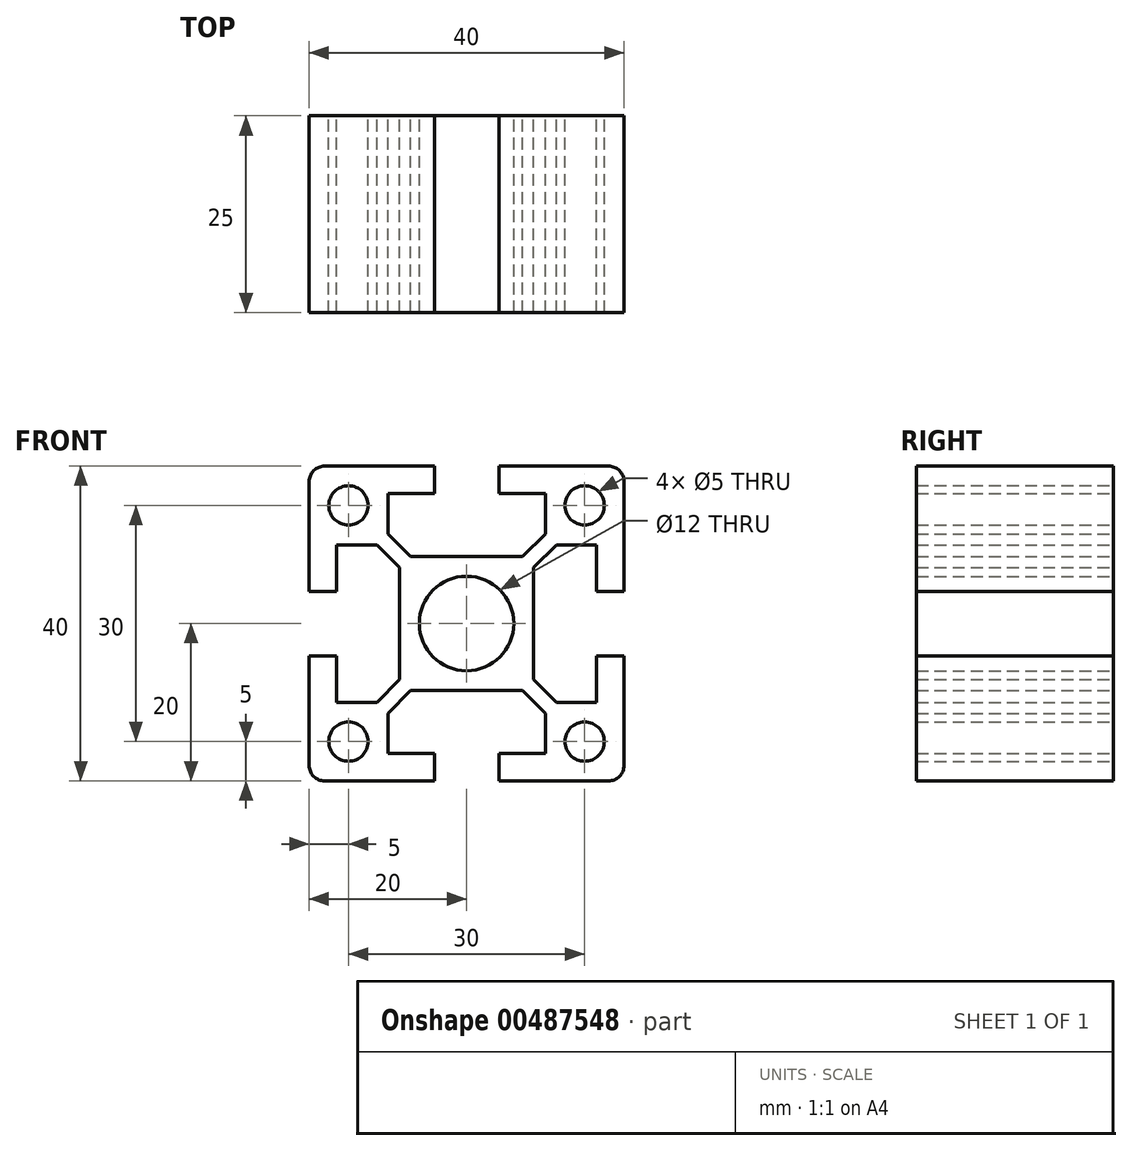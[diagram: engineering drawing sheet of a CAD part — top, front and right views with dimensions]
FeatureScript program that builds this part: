
annotation { "Feature Type Name" : "Feature", "Feature Type Description" : "" }
export const myFeature = defineFeature(function(context is Context, id is Id, definition is map)
    precondition{}
    {
        {
            var Q0;
            Q0=qCreatedBy(makeId("Front.planeOp"),FACE);
            var sketch = newSketch(context, id + "F0", { "sketchPlane" : qUnion([Q0])});
            skLineSegment(sketch, "E0.bottom", {"start": v(20, -20) * mm, "end": v(-20, -20) * mm});
            skLineSegment(sketch, "E0.top", {"start": v(20, 20) * mm, "end": v(-20, 20) * mm});
            skLineSegment(sketch, "E0.left", {"start": v(20, -20) * mm, "end": v(20, 20) * mm});
            skLineSegment(sketch, "E0.right", {"start": v(-20, -20) * mm, "end": v(-20, 20) * mm});
            skPoint(sketch, "E0.middle", {"position": v(0, 0) * mm});
            skCircle(sketch, "E1", {"center": v(0, 0) * mm, "radius": 6 * mm});
            skLineSegment(sketch, "E2", {"start": v(20, 15) * mm, "end": v(-20, 15) * mm, "construction": true});
            skLineSegment(sketch, "E3", {"start": v(20, -15) * mm, "end": v(-20, -15) * mm, "construction": true});
            skLineSegment(sketch, "E4", {"start": v(-15, -20) * mm, "end": v(-15, 20) * mm, "construction": true});
            skLineSegment(sketch, "E5", {"start": v(15, -20) * mm, "end": v(15, 20) * mm, "construction": true});
            skCircle(sketch, "E6", {"center": v(-15, 15) * mm, "radius": 2.5 * mm});
            skCircle(sketch, "E7", {"center": v(-15, -15) * mm, "radius": 2.5 * mm});
            skLineSegment(sketch, "E8", {"start": v(-4.1, 20) * mm, "end": v(-4.1, 16.5) * mm});
            skLineSegment(sketch, "E9", {"start": v(-4.1, 16.5) * mm, "end": v(-10, 16.5) * mm});
            skLineSegment(sketch, "E10", {"start": v(-10, 16.5) * mm, "end": v(-10, 11.4) * mm});
            skLineSegment(sketch, "E11", {"start": v(-10, 11.4) * mm, "end": v(-7.1, 8.5) * mm});
            skLineSegment(sketch, "E12", {"start": v(-7.1, 8.5) * mm, "end": v(0, 8.5) * mm});
            skLineSegment(sketch, "E13", {"start": v(0, 8.5) * mm, "end": v(0, 20) * mm});
            skLineSegment(sketch, "E14.MirrorCS", {"start": v(7.1, 8.5) * mm, "end": v(0, 8.5) * mm});
            skLineSegment(sketch, "E15.MirrorCS", {"start": v(10, 11.4) * mm, "end": v(7.1, 8.5) * mm});
            skLineSegment(sketch, "E16.MirrorCS", {"start": v(10, 16.5) * mm, "end": v(10, 11.4) * mm});
            skLineSegment(sketch, "E17.MirrorCS", {"start": v(4.1, 16.5) * mm, "end": v(10, 16.5) * mm});
            skLineSegment(sketch, "E18.MirrorCS", {"start": v(4.1, 20) * mm, "end": v(4.1, 16.5) * mm});
            skLineSegment(sketch, "E19.MirrorCS", {"start": v(7.1, -8.5) * mm, "end": v(0, -8.5) * mm});
            skLineSegment(sketch, "E20.MirrorCS", {"start": v(10, -11.4) * mm, "end": v(7.1, -8.5) * mm});
            skLineSegment(sketch, "E21.MirrorCS", {"start": v(10, -16.5) * mm, "end": v(10, -11.4) * mm});
            skLineSegment(sketch, "E22.MirrorCS", {"start": v(4.1, -16.5) * mm, "end": v(10, -16.5) * mm});
            skLineSegment(sketch, "E23.MirrorCS", {"start": v(4.1, -20) * mm, "end": v(4.1, -16.5) * mm});
            skLineSegment(sketch, "E24.MirrorCS", {"start": v(-4.1, -20) * mm, "end": v(-4.1, -16.5) * mm});
            skLineSegment(sketch, "E25.MirrorCS", {"start": v(-4.1, -16.5) * mm, "end": v(-10, -16.5) * mm});
            skLineSegment(sketch, "E26.MirrorCS", {"start": v(-10, -16.5) * mm, "end": v(-10, -11.4) * mm});
            skLineSegment(sketch, "E27.MirrorCS", {"start": v(-10, -11.4) * mm, "end": v(-7.1, -8.5) * mm});
            skLineSegment(sketch, "E28.MirrorCS", {"start": v(-7.1, -8.5) * mm, "end": v(0, -8.5) * mm});
            skCircle(sketch, "E29.MirrorC", {"center": v(15, -15) * mm, "radius": 2.5 * mm});
            skCircle(sketch, "E30.MirrorC", {"center": v(15, 15) * mm, "radius": 2.5 * mm});
            skLineSegment(sketch, "E31", {"start": v(-20, -4.1) * mm, "end": v(-16.5, -4.1) * mm});
            skLineSegment(sketch, "E32", {"start": v(-16.5, -4.1) * mm, "end": v(-16.5, -10) * mm});
            skLineSegment(sketch, "E33", {"start": v(-16.5, -10) * mm, "end": v(-11.4, -10) * mm});
            skLineSegment(sketch, "E34", {"start": v(-11.4, -10) * mm, "end": v(-8.5, -7.1) * mm});
            skLineSegment(sketch, "E35", {"start": v(-8.5, -7.1) * mm, "end": v(-8.5, 0) * mm});
            skLineSegment(sketch, "E36", {"start": v(-8.5, 0) * mm, "end": v(-20, 0) * mm});
            skLineSegment(sketch, "E37.MirrorCS", {"start": v(-8.5, 7.1) * mm, "end": v(-8.5, 0) * mm});
            skLineSegment(sketch, "E38.MirrorCS", {"start": v(-11.4, 10) * mm, "end": v(-8.5, 7.1) * mm});
            skLineSegment(sketch, "E39.MirrorCS", {"start": v(-16.5, 10) * mm, "end": v(-11.4, 10) * mm});
            skLineSegment(sketch, "E40.MirrorCS", {"start": v(-16.5, 4.1) * mm, "end": v(-16.5, 10) * mm});
            skLineSegment(sketch, "E41.MirrorCS", {"start": v(-20, 4.1) * mm, "end": v(-16.5, 4.1) * mm});
            skLineSegment(sketch, "E42.MirrorCS", {"start": v(8.5, 7.1) * mm, "end": v(8.5, 0) * mm});
            skLineSegment(sketch, "E43.MirrorCS", {"start": v(8.5, -7.1) * mm, "end": v(8.5, 0) * mm});
            skLineSegment(sketch, "E44.MirrorCS", {"start": v(11.4, -10) * mm, "end": v(8.5, -7.1) * mm});
            skLineSegment(sketch, "E45.MirrorCS", {"start": v(11.4, 10) * mm, "end": v(8.5, 7.1) * mm});
            skLineSegment(sketch, "E46.MirrorCS", {"start": v(16.5, 10) * mm, "end": v(11.4, 10) * mm});
            skLineSegment(sketch, "E47.MirrorCS", {"start": v(16.5, -10) * mm, "end": v(11.4, -10) * mm});
            skLineSegment(sketch, "E48.MirrorCS", {"start": v(16.5, -4.1) * mm, "end": v(16.5, -10) * mm});
            skLineSegment(sketch, "E49.MirrorCS", {"start": v(16.5, 4.1) * mm, "end": v(16.5, 10) * mm});
            skLineSegment(sketch, "E50.MirrorCS", {"start": v(20, 4.1) * mm, "end": v(16.5, 4.1) * mm});
            skLineSegment(sketch, "E51.MirrorCS", {"start": v(20, -4.1) * mm, "end": v(16.5, -4.1) * mm});
            skSolve(sketch);
        }
        {
            var Q0;
            Q0=makeQuery(id+"F0.imprint","IMPRINT",FACE,{"disambiguationData":[TD([[makeQuery(id+"F0.imprint","IMPRINT",EDGE,{"derivedFrom":sQuery(id+"F0.wireOp",EDGE,"E1")}),-1.0]])]});
            extrude(context, id + "F1", {"entities" : qUnion([Q0]), "depth" : 25 * mm});
        }
        {
            var Q0;
            Q0=makeQuery(id+"F1.opExtrude","SWEPT_EDGE",EDGE,{"disambiguationData":[OSD([sQuery(id+"F0.wireOp",EDGE,"E0.top"),sQuery(id+"F0.wireOp",EDGE,"E0.left")])]});
            var Q1;
            Q1=makeQuery(id+"F1.opExtrude","SWEPT_EDGE",EDGE,{"disambiguationData":[OSD([sQuery(id+"F0.wireOp",EDGE,"E0.top"),sQuery(id+"F0.wireOp",EDGE,"E0.right")])]});
            var Q2;
            Q2=makeQuery(id+"F1.opExtrude","SWEPT_EDGE",EDGE,{"disambiguationData":[OSD([sQuery(id+"F0.wireOp",EDGE,"E0.bottom"),sQuery(id+"F0.wireOp",EDGE,"E0.right")])]});
            var Q3;
            Q3=makeQuery(id+"F1.opExtrude","SWEPT_EDGE",EDGE,{"disambiguationData":[OSD([sQuery(id+"F0.wireOp",EDGE,"E0.bottom"),sQuery(id+"F0.wireOp",EDGE,"E0.left")])]});
            fillet(context, id + "F2", {"entities" : qUnion([Q0, Q1, Q2, Q3]), "radius" : 2 * mm, "tangentPropagation" : true, "allowEdgeOverflow" : false});
        }
    });
